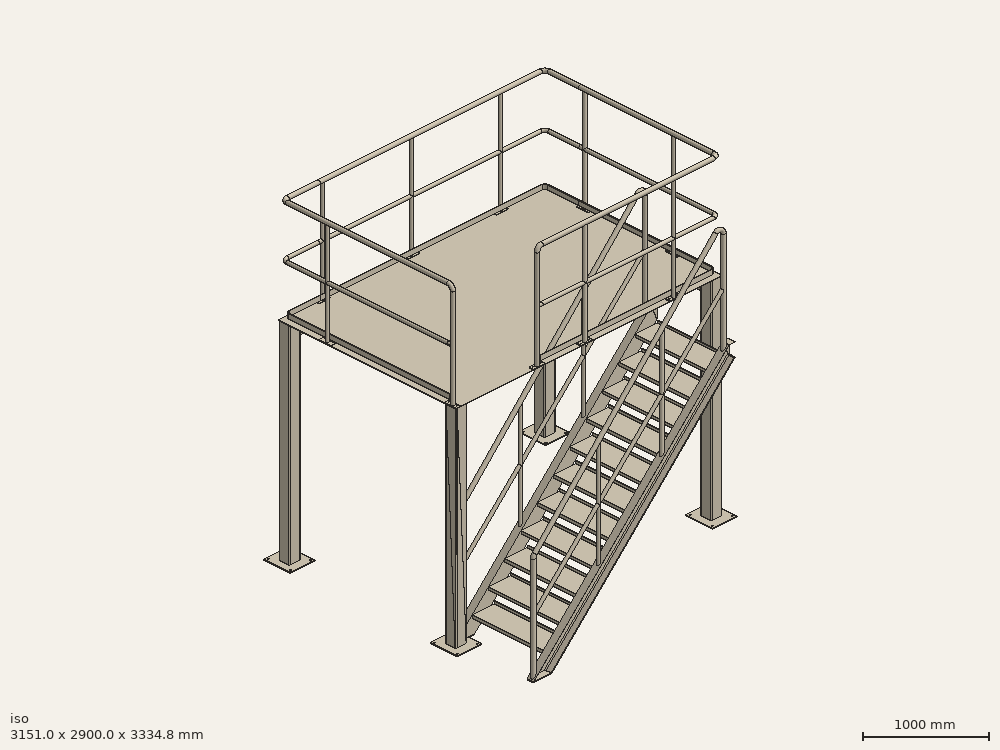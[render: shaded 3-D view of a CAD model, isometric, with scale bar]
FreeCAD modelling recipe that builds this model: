
FCSTD DOCUMENT  (FreeCAD 1.0R39319 (Git))
Label: trestle02
License: All rights reserved
objects: Part::FeaturePython×10, App::Part×3, Sketcher::SketchObject×2, Part::Feature×2, Spreadsheet::Sheet×1, Part::Extrusion×1, PartDesign::Pad×1, Part::MultiFuse×1
note: 21 computed .brp shape members not serialized (recipe doc carries the construction recipe); baked Part::Feature solids carry a one-line shape summary decoded from their .brp

FEATURE [Spreadsheet::Sheet] Spreadsheet
  cells = A1(key)='02; A2='W; B2(W0)=3000; A3='L; B3(L0)=2000; A4='H; B4(H0)=2200; A5='z1; B5(z1)=4.5
FEATURE [Sketcher::SketchObject] Sketch
  ArcFitTolerance = 0
  FullyConstrained = true
  MakeInternals = false
  expr: Constraints[8] = Spreadsheet.L0
  expr: Constraints[9] = Spreadsheet.W0
  sketch-geometry (4):
    g0: LineSegment StartX=-62.5 StartY=-62.5 StartZ=0 EndX=2937.5 EndY=-62.5 EndZ=0
    g1: LineSegment StartX=2937.5 StartY=-62.5 StartZ=0 EndX=2937.5 EndY=1937.5 EndZ=0
    g2: LineSegment StartX=2937.5 StartY=1937.5 StartZ=0 EndX=-62.5 EndY=1937.5 EndZ=0
    g3: LineSegment StartX=-62.5 StartY=1937.5 StartZ=0 EndX=-62.5 EndY=-62.5 EndZ=0
  constraints (12):
    c: Coincident(g0,g1)
    c: Coincident(g1,g2)
    c: Coincident(g2,g3)
    c: Coincident(g3,g0)
    c: Horizontal(g0)
    c: Horizontal(g2)
    c: Vertical(g1)
    c: Vertical(g3)
    c: DistanceY(g3,g3) = 2000
    c: DistanceX(g2,g2) = 3000
    c: DistanceY(g0,g-1) = 62.5
    c: DistanceX(g0,g-1) = 62.5
FEATURE [Part::Extrusion] Extrude001  label="chpl"
  Base = -> Sketch
  Dir = (0,0,1)
  DirMode = 2
  FaceMakerClass = Part::FaceMakerBullseye
  FaceMakerMode = 3
  JPN = 縞鋼板
  LengthFwd = 4.5
  LengthRev = 0
  Placement = pos=(0,0,2200) rot=(0,0,1;0rad)
  Solid = true
  Symmetric = false
  count = 1
  g0 = 7.85
  mass = 211.95
  material = SS41
  expr: .Placement.Base.z = Spreadsheet.H0
FEATURE [Part::FeaturePython] Corner001  # WARN: FeaturePython — macro-defined, semantics opaque (R4)
  JPN = てすり
  Placement = pos=(363,1913,2204.5) rot=(0,0,1;0rad)
  Reverse = true
  Standard = L1=2550.0,L2=400.0
  count = 1
  g0 = 7.85
  h = 1100
  k = -90
  l1 = 2550
  l2 = 400
  mass = 32.5879
  material = SS41
  p = 1000
  spec = 0
  type = 2
  expr: .Placement.Base.y = Spreadsheet.L0 - 87
  expr: .Placement.Base.z = Spreadsheet.H0 + 4.5
  expr: l1 = Spreadsheet.W0 - 450
FEATURE [Part::FeaturePython] Corner_with_end001  # WARN: FeaturePython — macro-defined, semantics opaque (R4)
  JPN = てすり
  Placement = pos=(877,-37,2204.5) rot=(0,0,1;0rad)
  Reverse = false
  Standard = L1=2036.0,L2=1550.0
  count = 1
  g0 = 7.85
  h = 1100
  k = 90
  l1 = 2036
  l2 = 1550
  mass = 44.8087
  material = SS41
  p = 1000
  spec = 0
  type = 1
  expr: .Placement.Base.z = Spreadsheet.H0 + 4.5
  expr: l1 = Spreadsheet.W0 - 1000 + 36
  expr: l2 = Spreadsheet.L0 - 450
FEATURE [Part::FeaturePython] Corner_with_end  # WARN: FeaturePython — macro-defined, semantics opaque (R4)
  JPN = てすり
  Placement = pos=(-36,-8e-15,2204.5) rot=(0,0,1;1.5708rad)
  Reverse = true
  Standard = L1=1913.0,L2=400.0
  count = 1
  g0 = 7.85
  h = 1100
  k = -90
  l1 = 1913
  l2 = 400
  mass = 25.6697
  material = SS41
  p = 1000
  spec = 0
  type = 1
  expr: .Placement.Base.z = Spreadsheet.H0 + 4.5
  expr: l1 = Spreadsheet.L0 - 100 + 13
FEATURE [Sketcher::SketchObject] Sketch001
  ArcFitTolerance = 1e-06
  FullyConstrained = true
  MakeInternals = false
  MapMode = 5
  Placement = pos=(0,0,0) rot=(1,0,0;3.14159rad)
  sketch-geometry (9):
    g0: LineSegment StartX=-138 StartY=-150 StartZ=0 EndX=138 EndY=-150 EndZ=0
    g1: LineSegment StartX=138 StartY=-150 StartZ=0 EndX=138 EndY=150 EndZ=0
    g2: LineSegment StartX=138 StartY=150 StartZ=0 EndX=-138 EndY=150 EndZ=0
    g3: LineSegment StartX=-138 StartY=150 StartZ=0 EndX=-138 EndY=-150 EndZ=0
    g4: GeomPoint [constr] X=-2e-16 Y=3e-16 Z=0
    g5: Circle CenterX=-113 CenterY=125 CenterZ=0 NormalX=0 NormalY=0 NormalZ=1 AngleXU=0 Radius=10
    g6: Circle CenterX=-113 CenterY=-125 CenterZ=0 NormalX=0 NormalY=0 NormalZ=1 AngleXU=0 Radius=10
    g7: Circle CenterX=113 CenterY=-125 CenterZ=0 NormalX=0 NormalY=0 NormalZ=1 AngleXU=0 Radius=10
    g8: Circle CenterX=113 CenterY=125 CenterZ=0 NormalX=0 NormalY=0 NormalZ=1 AngleXU=0 Radius=10
  constraints (24):
    c: Coincident(g0,g1)
    c: Coincident(g1,g2)
    c: Coincident(g2,g3)
    c: Coincident(g3,g0)
    c: Horizontal(g0)
    c: Horizontal(g2)
    c: Vertical(g1)
    c: Vertical(g3)
    c: Symmetric(g2,g0,g4)
    c: Coincident(g4,g-1)
    c: DistanceY(g-3,g1) = 50
    c: DistanceX(g-5,g0) = 50
    c: Diameter(g5) = 20
    c: Equal(g5,g6)
    c: Equal(g6,g7)
    c: Equal(g7,g8)
    c: Vertical(g5,g6)
    c: Vertical(g8,g7)
    c: Horizontal(g5,g8)
    c: Horizontal(g6,g7)
    c: DistanceY(g5,g2) = 25
    c: DistanceX(g2,g5) = 25
    c: DistanceX(g8,g1) = 25
    c: DistanceY(g0,g7) = 25
FEATURE [PartDesign::Pad] Pad  label="plt"
  Direction = (0,-1e-16,-1)
  Length = 9
  Length2 = 10
  Placement = pos=(0,0,0) rot=(1,0,0;3.14159rad)
  Profile = -> Sketch001
  ReferenceAxis = -> Sketch001 [N_Axis]
  Refine = true
  Suppressed = false
  Type = 0
FEATURE [Part::FeaturePython] SquarePipe  # WARN: FeaturePython — macro-defined, semantics opaque (R4)
  A = 125
  B = 125
  JPN = 角形鋼管
  L = 2200
  Placement = pos=(0,0,0) rot=(1,0,0;1.5708rad)
  Solid = true
  Standard = □200x200x6  L=500
  g0 = 7.85
  mass = 47.7221
  size = 40
  standard = SS
  t = 6
  type = 10_Square_Pipe
  expr: L = Spreadsheet.H0
FEATURE [App::Part] Part001  label="pst_SQ"
  Group = -> [Pad,Sketch001,SquarePipe]
  JPN = 支柱
  Origin = -> Origin001
  Standard = □125x125x6 , H=2200
  count = 1
  g0 = 7.85
  mass = 16.607
  material = SS41
FEATURE [Part::FeaturePython] Array  # Draft array (typed FeaturePython)
  Angle = 360
  ArrayType = 0
  Axis = (0,0,1)
  Base = -> Part001
  Center = (0,0,0)
  Count = 4
  Fuse = true
  IntervalAxis = (0,0,0)
  IntervalX = (2875,0,0)
  IntervalY = (0,1875,0)
  IntervalZ = (0,0,100)
  NumberCircles = 3
  NumberPolar = 5
  NumberX = 2
  NumberY = 2
  NumberZ = 1
  RadialDistance = 50
  Symmetry = 1
  TangentialDistance = 25
  expr: .IntervalX.x = Spreadsheet.W0 - 125
  expr: .IntervalY.y = Spreadsheet.L0 - 125
FEATURE [Part::FeaturePython] ChannelSteel  # WARN: FeaturePython — macro-defined, semantics opaque (R4)
  B = 75
  H = 150
  JPN = 溝形鋼
  L = 1750
  Placement = pos=(0,62.5,2125) rot=(0,0,1;0rad)
  Solid = true
  Standard = C150x75x6  L=5500
  g0 = 7.85
  mass = 92.9768
  size = 3
  standard = SS
  t1 = 6.5
  t2 = 10
  type = 01_Channel
  expr: .Placement.Base.z = Spreadsheet.H0 - 75
  expr: L = Spreadsheet.L0 - 250
FEATURE [Part::FeaturePython] Clone  label="ChannelSteel001"  # Draft clone (typed FeaturePython)
  AttacherType = Attacher::AttachEngine3D
  Fuse = false
  Objects = -> [ChannelSteel]
  Placement = pos=(2875,62.5,2125) rot=(0,0,1;0rad)
  Scale = (1,1,1)
  expr: .Placement.Base.x = Spreadsheet.W0 - 125
  expr: .Placement.Base.z = Spreadsheet.H0 - 75
FEATURE [Part::FeaturePython] ChannelSteel001  label="ChannelSteel002"  # WARN: FeaturePython — macro-defined, semantics opaque (R4)
  B = 75
  H = 150
  JPN = 溝形鋼
  L = 2750
  Placement = pos=(62.5,0,2125) rot=(0,0,1;4.71239rad)
  Solid = true
  Standard = C150x75x6  L=5500
  g0 = 7.85
  mass = 92.9768
  size = 3
  standard = SS
  t1 = 6.5
  t2 = 10
  type = 01_Channel
  expr: .Placement.Base.z = Spreadsheet.H0 - 75
  expr: L = Spreadsheet.W0 - 250
FEATURE [Part::FeaturePython] Clone001  label="ChannelSteel003"  # Draft clone (typed FeaturePython)
  AttacherType = Attacher::AttachEngine3D
  Fuse = false
  Objects = -> [ChannelSteel001]
  Placement = pos=(62.5,1875,2125) rot=(-0.707107,-0.707107,0;3.14159rad)
  Scale = (1,1,1)
  expr: .Placement.Base.y = Spreadsheet.L0 - 125
  expr: .Placement.Base.z = Spreadsheet.H0 - 75
FEATURE [Part::FeaturePython] SteelStair  # WARN: FeaturePython — macro-defined, semantics opaque (R4)
  H0 = 2200
  HighPlace = false
  JPN = 鋼製階段
  L = 2200
  L1 = 70
  Placement = pos=(106.066,0,-106.066) rot=(0,1,0;0rad)
  Position = 2
  body = 172.99
  handrail = 57.5144
  mass = 230.504
  size = 1
  t = 9
  type = 1
  w = 800
  expr: H0 = Spreadsheet.H0
  expr: L = Spreadsheet.H0
FEATURE [Part::Feature] SteelStair_Handrail_0
  Placement = pos=(30,0,30) rot=(0,1,0;0rad)
  shape: bbox 2194 x 42.7 x 3293 mm, 16 faces (baked)
FEATURE [Part::Feature] SteelStair_Handrail_1
  Placement = pos=(30,-880,30) rot=(0,1,0;0rad)
  shape: bbox 2194 x 42.7 x 3293 mm, 16 faces (baked)
FEATURE [Part::MultiFuse] SteelStair_HandrailFusion
  Refine = true
  Shapes = -> [SteelStair_Handrail_0,SteelStair_Handrail_1]
FEATURE [App::Part] SteelStair_Assy
  Group = -> [SteelStair,SteelStair_Handrail_0,SteelStair_Handrail_1,SteelStair_HandrailFusion]
  Origin = -> Origin002
  Placement = pos=(0,-2332,4.5) rot=(0,0,1;1.5708rad)
  expr: .Placement.Base.y = -(Spreadsheet.H0 + 132)
  expr: .Placement.Base.z = Spreadsheet.z1
FEATURE [App::Part] Part  label="trestleAssy"
  Group = -> [Spreadsheet,Sketch,Extrude001,Corner001,Corner_with_end001,Corner_with_end,Part001,Array,ChannelSteel,Clone,ChannelSteel001,Clone001,SteelStair_Assy]
  Origin = -> Origin
